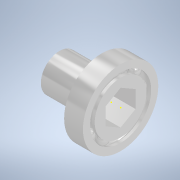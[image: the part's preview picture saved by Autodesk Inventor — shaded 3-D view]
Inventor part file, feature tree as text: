
AUTODESK INVENTOR PART (.ipt)
format: ipt  version: 2020.3 (Build 243373000, 373)  size: 305,664 bytes
history: native  units: mm
features: sketch x14, extrude x6, revolve x2, pattern_circular x1, projected_geometry x1
ambient origin geometry x8: Origin, YZ Plane, XZ Plane, XY Plane, X Axis, Y Axis, Z Axis, Center Point
bodies: Solid1 (feature_tree)
feature tree (24):
  sketch  "Sketch1"  dims[d6=8.0mm d7=3.0mm]
  sketch  "Sketch2"  dims[d8=8.0mm d9=3.0mm]
  revolve  "Revolution1"  [1 undecoded]
  sketch  "Sketch5"  dims[d10=2.0mm d11=8.0mm]
  sketch  "Sketch6"  dims[d12=6.0mm d13=1.0mm]
  sketch  "Sketch7"  dims[d15=90.0deg]
  revolve  "Revolution2"  [1 undecoded]
  pattern_circular  "Circular Pattern1"  Count=10 Angle=360.0deg
  sketch  "Sketch9"  dims[d17=90.0deg d18=100.0mm d19=360.0deg]
  sketch  "Sketch10"  dims[d21=8.0mm d22=0.0mm d23=15.75mm]
  extrude  "Extrusion1"  Depth=8.0mm
  extrude  "Extrusion2"  Depth=3.0mm TaperAngle=0.0deg
  extrude  "Extrusion3"  Depth=11.0mm TaperAngle=0.0deg
  extrude  "Extrusion4"  Depth=13.0mm TaperAngle=0.0deg
  extrude  "Extrusion5"  Depth=13.0mm TaperAngle=0.0deg
  extrude  "Extrusion6"  [1 undecoded]
  sketch  "Sketch8"  dims[d16=4.6mm]
  projected_geometry  "Projected Loop1"
  sketch  "Sketch11"  dims[d24=12.7mm d25=3.0mm d26=0.0mm]
  sketch  "Sketch12"  dims[d27=12.7mm d28=11.0mm d29=0.0mm]
  sketch  "Sketch13"  dims[d30=15.0mm d31=0.0mm d32=13.0mm d33=0.0mm]
  sketch  "Sketch14"  dims[d34=12.0mm d35=13.0mm d36=0.0mm]
  sketch  "Sketch15"
  sketch  "Sketch16"
note: 3 required parameter values undecoded (feature->parameter linkage not recoverable at this tier; creation-order binding heuristic only, values carry confidence <= 0.55)